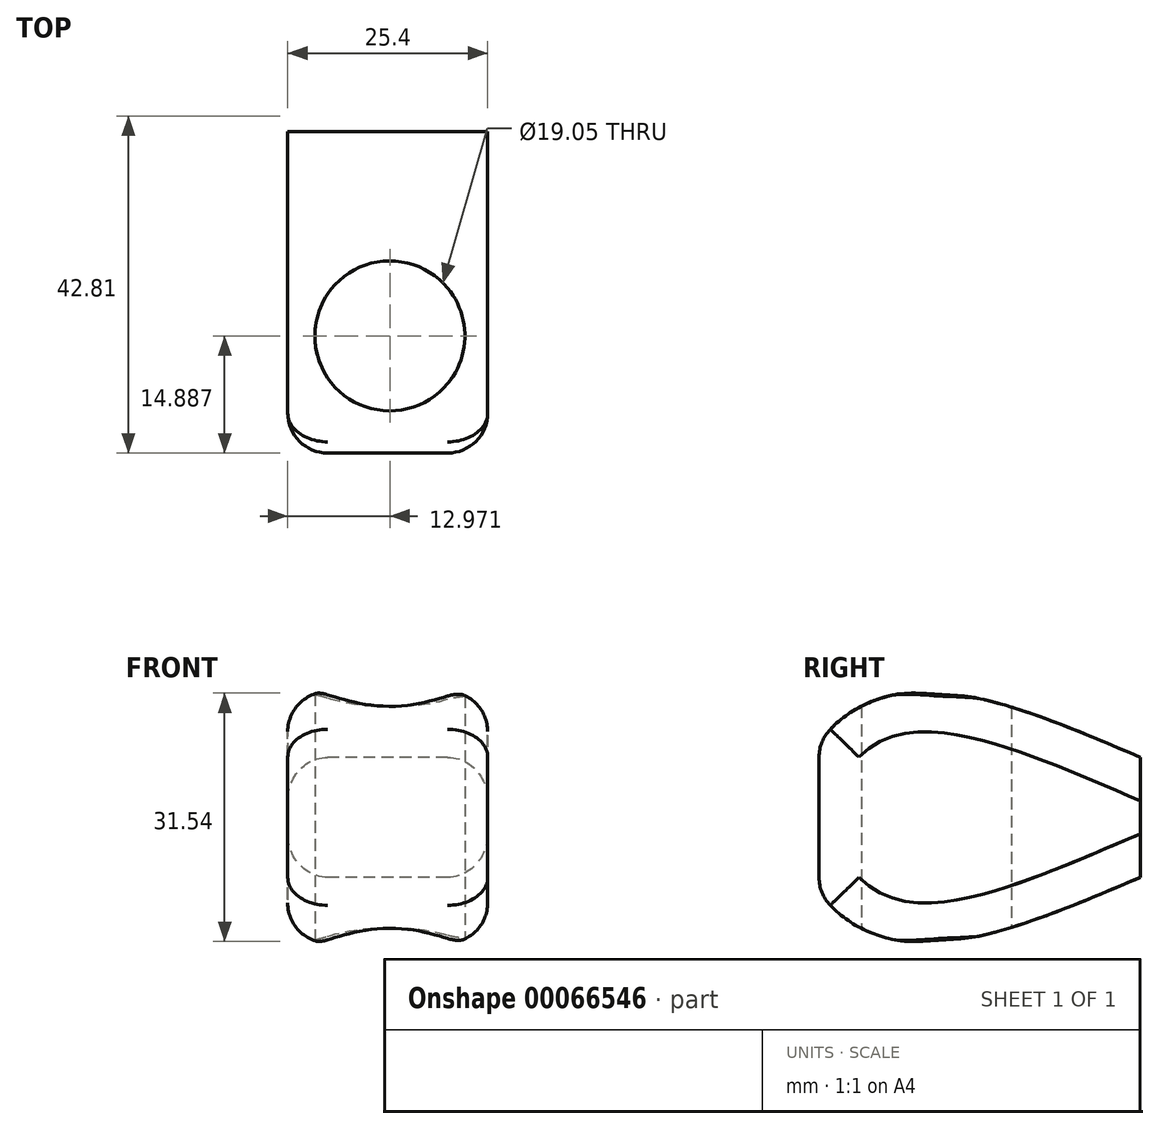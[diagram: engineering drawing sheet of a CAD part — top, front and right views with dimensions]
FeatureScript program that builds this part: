
annotation { "Feature Type Name" : "Feature", "Feature Type Description" : "" }
export const myFeature = defineFeature(function(context is Context, id is Id, definition is map)
    precondition{}
    {
        {
            var Q0;
            Q0=qCreatedBy(makeId("Right.planeOp"),FACE);
            var sketch = newSketch(context, id + "F0", { "sketchPlane" : qUnion([Q0])});
            skLineSegment(sketch, "E0.bottom", {"start": v(-11.62, 38.13) * mm, "end": v(30.29, 38.13) * mm, "construction": true});
            skLineSegment(sketch, "E0.top", {"start": v(-11.62, 6.38) * mm, "end": v(30.29, 6.38) * mm, "construction": true});
            skLineSegment(sketch, "E0.left", {"start": v(-11.62, 38.13) * mm, "end": v(-11.62, 6.38) * mm, "construction": true});
            skLineSegment(sketch, "E0.right", {"start": v(30.29, 38.13) * mm, "end": v(30.29, 6.38) * mm, "construction": true});
            skLineSegment(sketch, "E1.0", {"start": v(-11.62, 29.87) * mm, "end": v(30.29, 29.87) * mm, "construction": true});
            skLineSegment(sketch, "E2.0", {"start": v(-11.62, 14.63) * mm, "end": v(30.29, 14.63) * mm, "construction": true});
            skLineSegment(sketch, "E3.0", {"start": v(1.08, 38.13) * mm, "end": v(1.08, 6.38) * mm, "construction": true});
            skFitSpline(sketch, "E4", {"points": [v(30.29, 29.87) * mm, v(1.08, 38.13) * mm, v(-11.62, 29.87) * mm, v(-11.62, 14.63) * mm, v(1.08, 6.38) * mm, v(30.29, 14.63) * mm], "startDerivative": vector(-130.01, 55.64) * mm, "endDerivative": vector(130.01, 55.64) * mm});
            skLineSegment(sketch, "E5", {"start": v(30.29, 29.87) * mm, "end": v(30.29, 14.63) * mm});
            skSolve(sketch);
        }
        {
            var Q0;
            Q0=makeQuery(id+"F0.imprint","IMPRINT",FACE,{"disambiguationData":[TD([[makeQuery(id+"F0.imprint","IMPRINT",EDGE,{"derivedFrom":sQuery(id+"F0.wireOp",EDGE,"E4")}),1.0]])]});
            extrude(context, id + "F1", {"entities" : qUnion([Q0]), "depth" : 25.4 * mm});
        }
        {
            var Q0;
            Q0=qCreatedBy(makeId("Top.planeOp"),FACE);
            var sketch = newSketch(context, id + "F2", { "sketchPlane" : qUnion([Q0])});
            skCircle(sketch, "E6", {"center": v(12.97, 4.37) * mm, "radius": 9.53 * mm});
            skSolve(sketch);
        }
        {
            var Q0;
            Q0=makeQuery(id+"F2.imprint","IMPRINT",FACE,{"disambiguationData":[TD([[makeQuery(id+"F2.imprint","IMPRINT",EDGE,{"derivedFrom":sQuery(id+"F2.wireOp",EDGE,"E6")}),1.0]])]});
            extrude(context, id + "F3", {"entities" : qUnion([Q0]), "depth" : 2.54 * mm});
        }
        {
            var Q0;
            Q0=makeQuery(id+"F3.opExtrude","CAP_FACE",FACE,{"disambiguationData":[OSD([sQuery(id+"F2.wireOp",EDGE,"E6")])],"isStart":true});
            var sketch = newSketch(context, id + "F4", { "sketchPlane" : qUnion([Q0])});
            skSolve(sketch);
        }
        {
            var Q0;
            Q0=qSketchRegion(id+"F4",true);
            var Q1;
            Q1=makeQuery(id+"F4.imprint","IMPRINT",FACE,{"disambiguationData":[TD([[makeQuery(id+"F4.imprint","IMPRINT",EDGE,{"derivedFrom":makeQuery(id+"F3.opExtrude","CAP_EDGE",EDGE,{"disambiguationData":[OSD([sQuery(id+"F2.wireOp",EDGE,"E6")])],"isStart":true})}),-1.0]])]});
            extrude(context, id + "F5", {"entities" : qUnion([Q0, Q1]), "operationType" : NewBodyOperationType.REMOVE, "endBound" : BoundingType.THROUGH_ALL, "oppositeDirection" : true, "depth" : 25.4 * mm});
        }
        {
            var Q0;
            Q0=makeQuery(id+"F1.opExtrude","CAP_FACE",FACE,{"disambiguationData":[OSD([sQuery(id+"F0.wireOp",EDGE,"E4"),sQuery(id+"F0.wireOp",EDGE,"E5")])],"isStart":true});
            var sketch = newSketch(context, id + "F6", { "sketchPlane" : qUnion([Q0])});
            skLineSegment(sketch, "E7.bottom", {"start": v(10.52, 31.7) * mm, "end": v(38.7, 31.7) * mm});
            skLineSegment(sketch, "E7.top", {"start": v(10.52, 12.66) * mm, "end": v(38.7, 12.66) * mm});
            skLineSegment(sketch, "E7.left", {"start": v(10.52, 31.7) * mm, "end": v(10.52, 12.66) * mm});
            skLineSegment(sketch, "E7.right", {"start": v(38.7, 31.7) * mm, "end": v(38.7, 12.66) * mm});
            skSolve(sketch);
        }
        {
            var Q0;
            Q0=qSketchRegion(id+"F6",true);
            extrude(context, id + "F7", {"entities" : qUnion([Q0]), "operationType" : NewBodyOperationType.REMOVE, "endBound" : BoundingType.THROUGH_ALL, "oppositeDirection" : true, "depth" : 25.4 * mm});
        }
        {
            var Q0;
            Q0=makeQuery(id+"F7.boolean.opBoolean","SPLIT",EDGE,{"disambiguationData":[OD(0.0)],"derivedFrom":makeQuery(id+"F1.opExtrude","CAP_EDGE",EDGE,{"disambiguationData":[OSD([sQuery(id+"F0.wireOp",EDGE,"E4")])],"isStart":false})});
            var Q1;
            Q1=makeQuery(id+"F7.boolean.opBoolean","SPLIT",EDGE,{"disambiguationData":[OD(0.0)],"derivedFrom":makeQuery(id+"F1.opExtrude","CAP_EDGE",EDGE,{"disambiguationData":[OSD([sQuery(id+"F0.wireOp",EDGE,"E4")])],"isStart":true})});
            var Q2;
            Q2=makeQuery(id+"F7.boolean.opBoolean","SPLIT",EDGE,{"disambiguationData":[OD(1.0)],"derivedFrom":makeQuery(id+"F1.opExtrude","CAP_EDGE",EDGE,{"disambiguationData":[OSD([sQuery(id+"F0.wireOp",EDGE,"E4")])],"isStart":false})});
            var Q3;
            Q3=makeQuery(id+"F7.boolean.opBoolean","SPLIT",EDGE,{"disambiguationData":[OD(1.0)],"derivedFrom":makeQuery(id+"F1.opExtrude","CAP_EDGE",EDGE,{"disambiguationData":[OSD([sQuery(id+"F0.wireOp",EDGE,"E4")])],"isStart":true})});
            fillet(context, id + "F8", {"entities" : qUnion([Q0, Q1, Q2, Q3]), "radius" : 5.08 * mm, "tangentPropagation" : true, "allowEdgeOverflow" : false});
        }
        {
            var Q0;
            Q0=makeQuery(id+"F8.opFillet","BLEND_EDGE",EDGE,{"blendedFrom":[makeQuery(id+"F7.boolean.opBoolean","SPLIT",EDGE,{"disambiguationData":[OD(0.0)],"derivedFrom":makeQuery(id+"F1.opExtrude","CAP_EDGE",EDGE,{"disambiguationData":[OSD([sQuery(id+"F0.wireOp",EDGE,"E4")])],"isStart":true})}),makeQuery(id+"F7.boolean.opBoolean","COPY",FACE,{"derivedFrom":makeQuery(id+"F7.opExtrude","SWEPT_FACE",FACE,{"disambiguationData":[OSD([sQuery(id+"F6.wireOp",EDGE,"E7.left")])]})})],"blendedInto":[makeQuery(id+"F7.boolean.opBoolean","COPY",FACE,{"derivedFrom":makeQuery(id+"F7.opExtrude","SWEPT_FACE",FACE,{"disambiguationData":[OSD([sQuery(id+"F6.wireOp",EDGE,"E7.left")])]})})]});
            fillet(context, id + "F9", {"entities" : qUnion([Q0]), "radius" : 5.08 * mm, "tangentPropagation" : true, "allowEdgeOverflow" : false});
        }
    });
